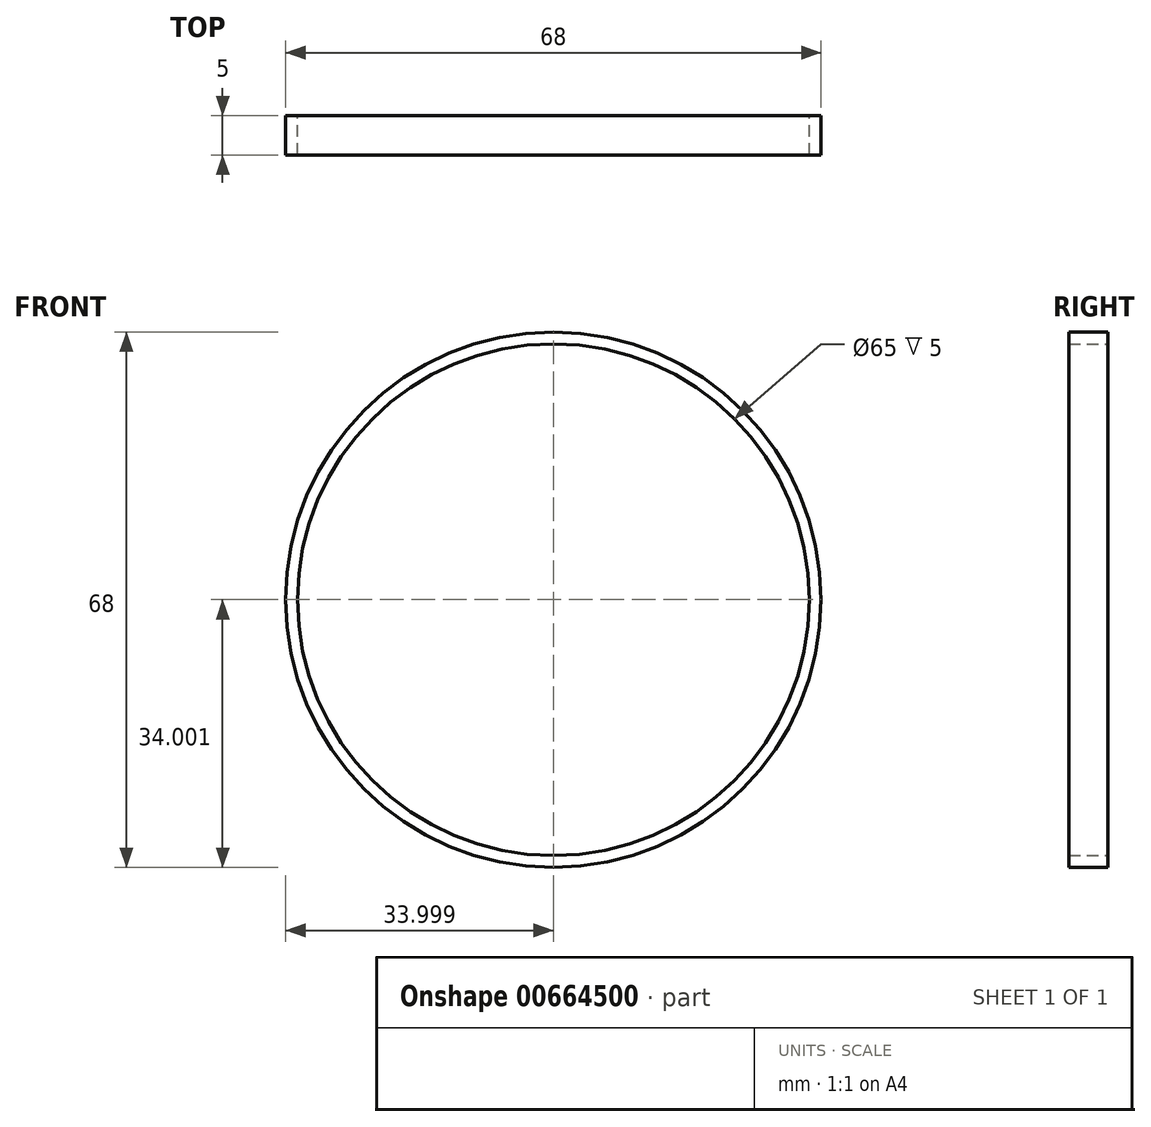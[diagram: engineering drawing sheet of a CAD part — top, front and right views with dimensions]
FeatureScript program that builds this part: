
annotation { "Feature Type Name" : "Feature", "Feature Type Description" : "" }
export const myFeature = defineFeature(function(context is Context, id is Id, definition is map)
    precondition{}
    {
        {
            var Q0;
            Q0=qCreatedBy(makeId("Front.planeOp"),FACE);
            var sketch = newSketch(context, id + "F0", { "sketchPlane" : qUnion([Q0])});
            skPoint(sketch, "E0.0", {"position": v(0.02, -15.8) * mm});
            skCircle(sketch, "E1", {"center": v(-0.71, 18.2) * mm, "radius": 34 * mm});
            skCircle(sketch, "E2", {"center": v(-0.71, 18.2) * mm, "radius": 32.5 * mm});
            skSolve(sketch);
        }
        {
            var Q0;
            Q0=makeQuery(id+"F0.imprint","IMPRINT",FACE,{"disambiguationData":[TD([[makeQuery(id+"F0.imprint","IMPRINT",EDGE,{"derivedFrom":sQuery(id+"F0.wireOp",EDGE,"E1")}),1.0]])]});
            extrude(context, id + "F1", {"entities" : qUnion([Q0]), "depth" : 5 * mm, "offsetDistance" : 25 * mm});
        }
    });
